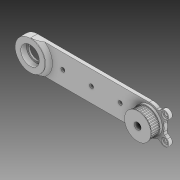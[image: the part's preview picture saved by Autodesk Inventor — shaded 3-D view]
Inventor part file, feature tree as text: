
AUTODESK INVENTOR PART (.ipt)
format: ipt  version: 2020 (Build 240168000, 168)  size: 423,936 bytes
history: native  units: mm
features: extrude x9, sketch x9, chamfer x2, plane x1, revolve x1, fillet x1, projected_geometry x1
ambient origin geometry x8: Origin, YZ Plane, XZ Plane, XY Plane, X Axis, Y Axis, Z Axis, Center Point
bodies: Solid1 (feature_tree)
feature tree (24):
  extrude  "Extrusion1"  Depth=13.0mm
  extrude  "Extrusion2"  Depth=6.0mm
  extrude  "Extrusion5"  Depth=10.0mm TaperAngle=0.0deg
  extrude  "Extrusion6"  Depth=25.0mm
  extrude  "Extrusion7"  Depth=25.0mm
  chamfer  "Chamfer2"  Distance=3.5mm
  plane  "Work Plane1"
  extrude  "Extrusion8"  Depth=1.5mm
  chamfer  "Chamfer3"  Distance=0.2mm
  revolve  "Revolution1"  [1 undecoded]
  extrude  "Extrusion10"  Depth=2.0mm
  fillet  "Fillet1"  Radius=1.74133mm
  extrude  "Extrusion11"  Depth=9.0mm
  extrude  "Extrusion14"  Depth=9.0mm TaperAngle=360.0deg
  sketch  "Sketch1"  dims[d0=13.0mm d1=100.3mm]
  sketch  "Sketch2"  dims[d2=3.0mm d3=0.0mm d4=6.0mm]
  sketch  "Sketch5"  dims[d6=16.3mm d7=10.0mm d8=0.0mm]
  sketch  "Sketch6"  dims[d18=3.5mm d19=25.0mm]
  sketch  "Sketch7"  dims[d20=25.0mm d21=16.25mm d22=3.5mm d23=0.0mm]
  projected_geometry  "Projected Loop1"
  sketch  "Sketch8"  dims[d24=5.0mm d25=0.0mm d26=1.5mm d27=0.2mm d28=0.0mm]
  sketch  "Sketch12"  dims[d29=3.0mm d30=2.0mm d31=45.0deg d32=23.0mm]
  sketch  "Sketch13"  dims[d33=-1.0mm d34=2.0mm d35=1.74133mm]
  sketch  "Sketch16"  dims[d36=1.2mm d37=0.65mm d38=360.0mm d40=360.0deg d42=7.0mm d43=0.0mm d44=0.6mm d45=2.0mm d46=45.0deg d60=90.0deg d61=3.2mm d62=7.5mm d64=10.0mm d65=10.0mm d66=0.0mm d67=2.0mm d68=6.0mm d69=1.5mm d70=0.0mm d91=8.1mm d92=9.0mm d93=0.0mm d71=0.872665mm]
note: 1 required parameter value undecoded (feature->parameter linkage not recoverable at this tier; creation-order binding heuristic only, values carry confidence <= 0.55)
